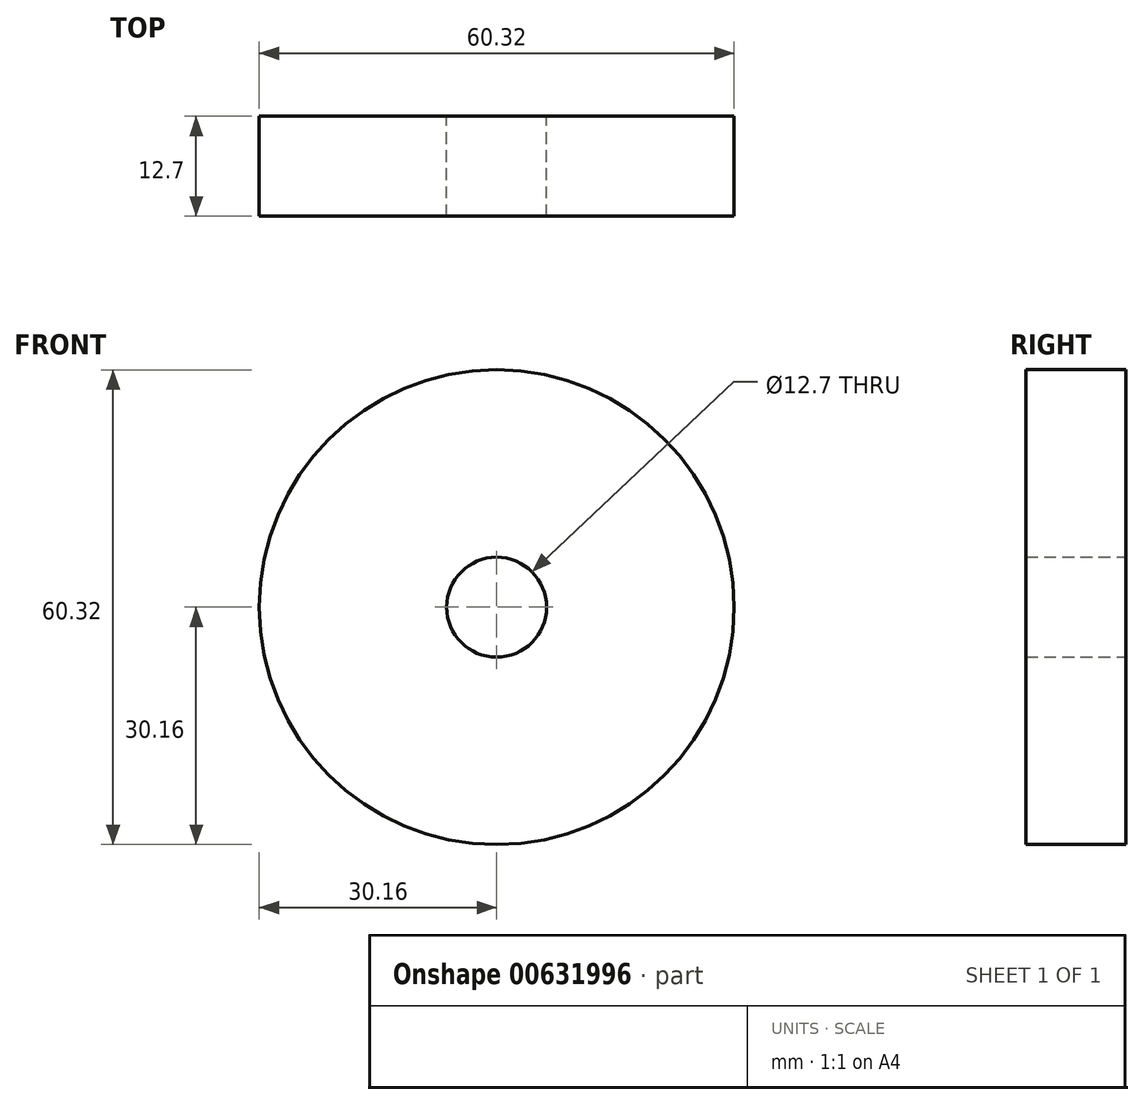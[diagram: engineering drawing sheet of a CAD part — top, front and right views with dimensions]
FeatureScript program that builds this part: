
annotation { "Feature Type Name" : "Feature", "Feature Type Description" : "" }
export const myFeature = defineFeature(function(context is Context, id is Id, definition is map)
    precondition{}
    {
        {
            var Q0;
            Q0=qCreatedBy(makeId("Front.planeOp"),FACE);
            var sketch = newSketch(context, id + "F0", { "sketchPlane" : qUnion([Q0])});
            skCircle(sketch, "E0", {"center": v(0, 0) * mm, "radius": 30.16 * mm});
            skCircle(sketch, "E1", {"center": v(0, 0) * mm, "radius": 6.35 * mm});
            skSolve(sketch);
        }
        {
            var Q0;
            Q0=makeQuery(id+"F0.imprint","IMPRINT",FACE,{"disambiguationData":[TD([[makeQuery(id+"F0.imprint","IMPRINT",EDGE,{"derivedFrom":sQuery(id+"F0.wireOp",EDGE,"E0")}),1.0]])]});
            extrude(context, id + "F1", {"entities" : qUnion([Q0]), "depth" : 12.7 * mm, "offsetDistance" : 25.4 * mm});
        }
    });
